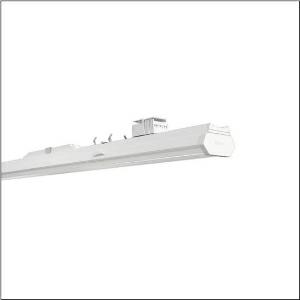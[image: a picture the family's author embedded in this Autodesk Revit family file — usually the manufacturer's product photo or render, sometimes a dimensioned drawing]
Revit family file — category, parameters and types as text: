
# Revit family: licross_r__11_protected_ho_51tp12mn4f5m_a747
name_source: partatom
category: Lighting Fixtures
units: mm (PartAtom-declared; Revit-internal decimal feet)

## family parameters
Cut with Voids When Loaded = No
Host = Face
Light Source = No
Part Type = Normal
Room Calculation Point = No
Round Connector Dimension = Use Diameter
Shared = No

## types (1)
- --- (1 x LED, 15820 lm, 87.4 W, 4000K)
    Apparent Load = 87 VA
    CIE Flux Codes = 70 91 97 98 100
    Color Rendering = 80
    Color Temperature = 4000K
    Default Elevation = 1800 mm
    Description = Licross® 11 Protected HO, luminaire insert, of sheet steel, galvanised, coil coated, white, length: 1.500mm, width: 90mm, height: 101mm, LED rated luminous flux: 15.820lm, light colour: 840, control gear: ON/OFF Multilumen, control gear: ECG Multilumen, with plug, 3-pole, with phase selection, mains connection: 220..240V, AC, 50/60Hz, halogen-free wiring, primary light control with lens, of plastic, primary optical cover: cover, of PMMA, light emission: direct with ceiling illumination distribution, primary light characteristic: symmetric, protection rating (complete): IP64, insulation class (complete): insulation class I (protective earthing), certification: CE, ENEC, VDE, UKCA, protection symbol: D if used in an environment with conductive dust loads with corresponding accessories, impact resistance: IK06, permissible ambient temperature for indoor applications: -35..+35°C, corresponds to IFS (International Featured Standards) requirements for safety and quality in the food industry, reducing of maximum allowable ambient temperature of 5°C with ceiling mounting, LABS conformity tested according to VDMA 24364:2018-05, packaging unit: 1 piece
    Height = 92 mm
    Lamp = 1 x LED
    Lamp Light Flux = 15820 lm
    Lamp Power = 87.4 W
    Lamp count = 1
    Length = 1500 mm
    Luminous efficacy = 181 lm/W
    Manufacturer = Siteco
    ModVariant = No
    Model = 51TP12MN4F5M
    Mounting Place = Ceiling
    Mounting Type = Pendant
    Number of Poles = 1
    OnlyDefault = Yes
    Power Factor = 1
    Product Name = Licross® 11 Protected HO
    Product group = luminaire insert
    ProductGroupID = 902
    Protection Class = Protection class I
    Protection Degree = IP 64
    RLX_Detail_Level = 1
    RlxData = <blob elided: 22085 chars, md5=f1cf0cc8>
    Socket = socket
    Standby Power = 0 W
    System Light Flux = 15820 lm
    System Power = 87 W
    Type Comments = factory setting: luminous flux: 100 % | (A | C | E) | 203 mA
    Type Image = l_1256148.jpg
    URL = http://relux.com
    VarID = @adj_003919
    Voltage = 0 V
    Weight = 0.00 kg
    Width = 88 mm

## geometry (parser evidence)
native form markers: Blend x4, Sweep x12
no freeform markers — native parametric forms only
